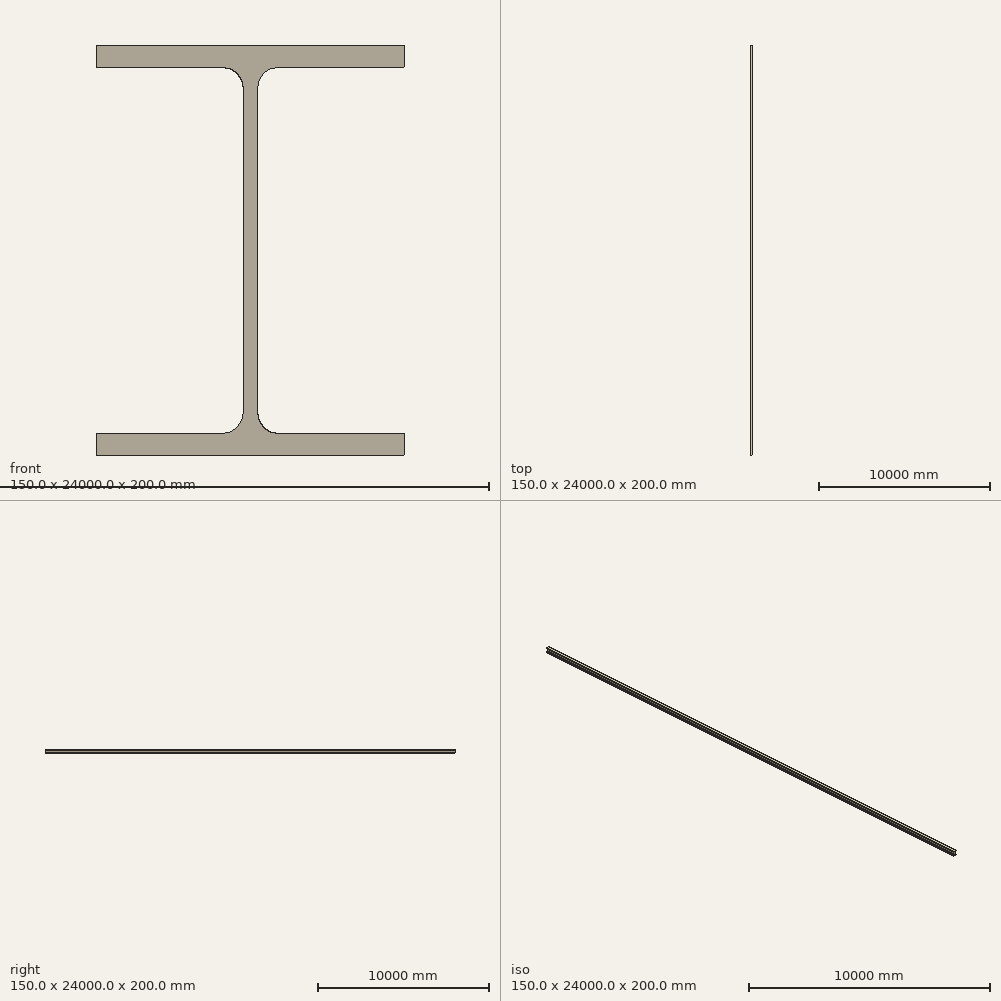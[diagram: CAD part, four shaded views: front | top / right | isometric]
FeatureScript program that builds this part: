
annotation { "Feature Type Name" : "Feature", "Feature Type Description" : "" }
export const myFeature = defineFeature(function(context is Context, id is Id, definition is map)
    precondition{}
    {
        {
            var Q0;
            Q0=qCreatedBy(makeId("Front.planeOp"),FACE);
            var sketch = newSketch(context, id + "F0", { "sketchPlane" : qUnion([Q0])});
            skLineSegment(sketch, "E0.left", {"start": v(3.55, 79.3) * mm, "end": v(3.55, -79.3) * mm});
            skLineSegment(sketch, "E0.right", {"start": v(-3.55, 79.3) * mm, "end": v(-3.55, -79.3) * mm});
            skPoint(sketch, "E0.middle", {"position": v(0, 0) * mm});
            skLineSegment(sketch, "E1.bottom", {"start": v(-75, 89.3) * mm, "end": v(-13.55, 89.3) * mm});
            skLineSegment(sketch, "E1.top", {"start": v(-75, 100) * mm, "end": v(75, 100) * mm});
            skLineSegment(sketch, "E1.left", {"start": v(-75, 89.3) * mm, "end": v(-75, 100) * mm});
            skLineSegment(sketch, "E1.right", {"start": v(75, 89.3) * mm, "end": v(75, 100) * mm});
            skLineSegment(sketch, "E2.bottom", {"start": v(75, -89.3) * mm, "end": v(13.55, -89.3) * mm});
            skLineSegment(sketch, "E2.top", {"start": v(75, -100) * mm, "end": v(-75, -100) * mm});
            skLineSegment(sketch, "E2.left", {"start": v(75, -89.3) * mm, "end": v(75, -100) * mm});
            skLineSegment(sketch, "E2.right", {"start": v(-75, -89.3) * mm, "end": v(-75, -100) * mm});
            skLineSegment(sketch, "E3.trimOffspring", {"start": v(13.55, 89.3) * mm, "end": v(75, 89.3) * mm});
            skLineSegment(sketch, "E4.trimOffspring", {"start": v(-13.55, -89.3) * mm, "end": v(-75, -89.3) * mm});
            skPoint(sketch, "E5.visualSharp", {"position": v(3.55, 89.3) * mm});
            skArc(sketch, "E5.filletArc", {"start": v(13.55, 89.3) * mm, "mid": v(6.48, 86.37) * mm, "end": v(3.55, 79.3) * mm});
            skPoint(sketch, "E6.visualSharp", {"position": v(-3.55, 89.3) * mm});
            skArc(sketch, "E6.filletArc", {"start": v(-3.55, 79.3) * mm, "mid": v(-6.48, 86.37) * mm, "end": v(-13.55, 89.3) * mm});
            skPoint(sketch, "E7.visualSharp", {"position": v(3.55, -89.3) * mm});
            skArc(sketch, "E7.filletArc", {"start": v(3.55, -79.3) * mm, "mid": v(6.48, -86.37) * mm, "end": v(13.55, -89.3) * mm});
            skPoint(sketch, "E8.visualSharp", {"position": v(-3.55, -89.3) * mm});
            skArc(sketch, "E8.filletArc", {"start": v(-13.55, -89.3) * mm, "mid": v(-6.48, -86.37) * mm, "end": v(-3.55, -79.3) * mm});
            skSolve(sketch);
        }
        {
            var Q0;
            Q0=qSketchRegion(id+"F0",true);
            extrude(context, id + "F1", {"entities" : qUnion([Q0]), "oppositeDirection" : true, "depth" : 24000 * mm});
        }
    });
